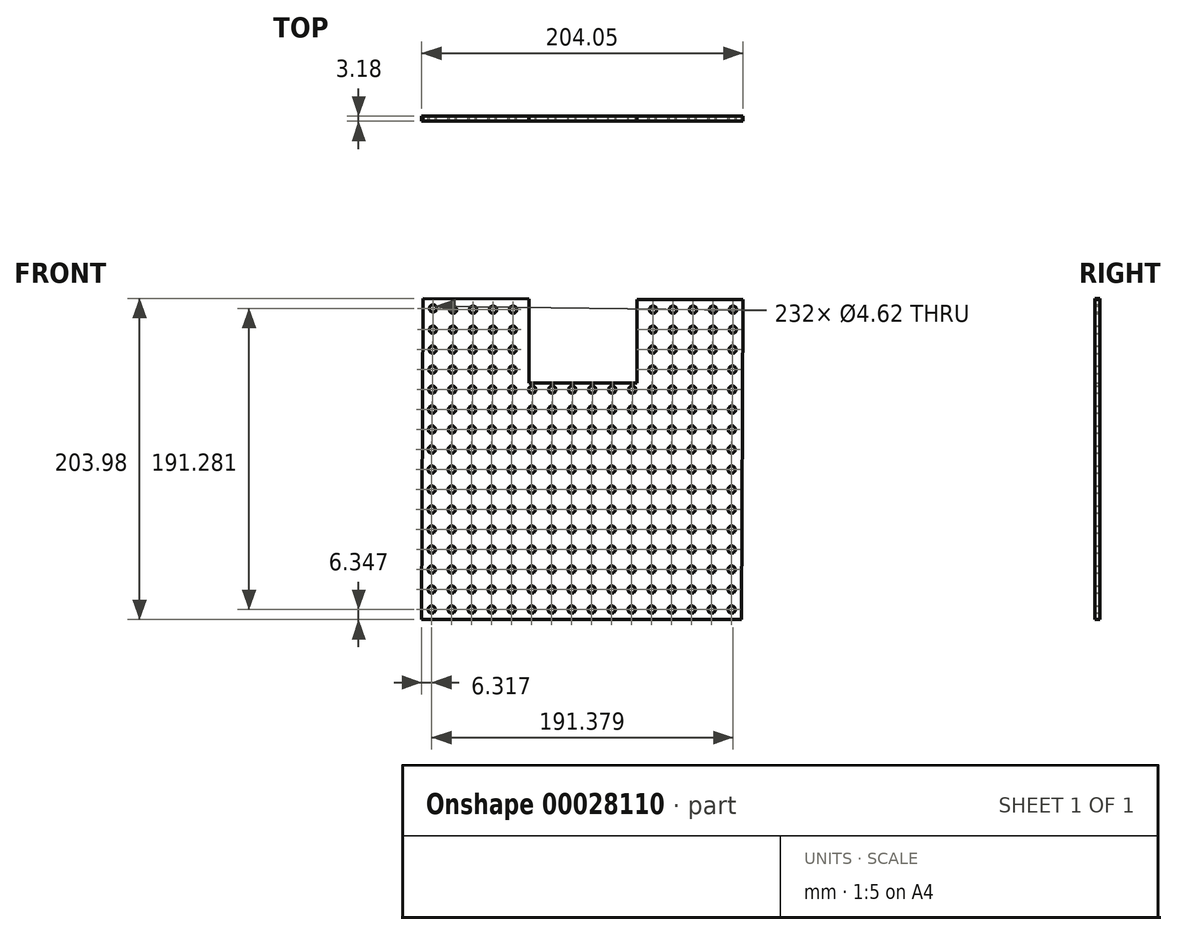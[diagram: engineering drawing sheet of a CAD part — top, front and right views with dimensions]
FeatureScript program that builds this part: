
annotation { "Feature Type Name" : "Feature", "Feature Type Description" : "" }
export const myFeature = defineFeature(function(context is Context, id is Id, definition is map)
    precondition{}
    {
        {
            var Q0;
            Q0=qCreatedBy(makeId("Front.planeOp"),FACE);
            var sketch = newSketch(context, id + "F0", { "sketchPlane" : qUnion([Q0])});
            skCircle(sketch, "E0", {"center": v(-1.82, 8.54) * mm, "radius": 2.31 * mm});
            skCircle(sketch, "E1.1.0.0", {"center": v(-14.52, 8.54) * mm, "radius": 2.31 * mm});
            skCircle(sketch, "E1.2.0.0", {"center": v(-27.22, 8.54) * mm, "radius": 2.31 * mm});
            skCircle(sketch, "E1.3.0.0", {"center": v(-39.92, 8.54) * mm, "radius": 2.31 * mm});
            skCircle(sketch, "E1.4.0.0", {"center": v(-52.62, 8.54) * mm, "radius": 2.31 * mm});
            skLineSegment(sketch, "E1.direction1", {"start": v(-1.82, 8.54) * mm, "end": v(-14.52, 8.54) * mm, "construction": true});
            skCircle(sketch, "E2.1.0.0", {"center": v(-1.95, -4.16) * mm, "radius": 2.31 * mm});
            skCircle(sketch, "E2.1.0.1", {"center": v(-14.65, -4.16) * mm, "radius": 2.31 * mm});
            skCircle(sketch, "E2.1.0.2", {"center": v(-27.35, -4.16) * mm, "radius": 2.31 * mm});
            skCircle(sketch, "E2.1.0.3", {"center": v(-40.05, -4.16) * mm, "radius": 2.31 * mm});
            skCircle(sketch, "E2.1.0.4", {"center": v(-52.75, -4.16) * mm, "radius": 2.31 * mm});
            skCircle(sketch, "E2.2.0.0", {"center": v(-2.08, -16.86) * mm, "radius": 2.31 * mm});
            skCircle(sketch, "E2.2.0.1", {"center": v(-14.78, -16.86) * mm, "radius": 2.31 * mm});
            skCircle(sketch, "E2.2.0.2", {"center": v(-27.48, -16.86) * mm, "radius": 2.31 * mm});
            skCircle(sketch, "E2.2.0.3", {"center": v(-40.18, -16.86) * mm, "radius": 2.31 * mm});
            skCircle(sketch, "E2.2.0.4", {"center": v(-52.88, -16.86) * mm, "radius": 2.31 * mm});
            skCircle(sketch, "E2.3.0.0", {"center": v(-2.2, -29.56) * mm, "radius": 2.31 * mm});
            skCircle(sketch, "E2.3.0.1", {"center": v(-14.9, -29.56) * mm, "radius": 2.31 * mm});
            skCircle(sketch, "E2.3.0.2", {"center": v(-27.6, -29.56) * mm, "radius": 2.31 * mm});
            skCircle(sketch, "E2.3.0.3", {"center": v(-40.3, -29.56) * mm, "radius": 2.31 * mm});
            skCircle(sketch, "E2.3.0.4", {"center": v(-53, -29.56) * mm, "radius": 2.31 * mm});
            skCircle(sketch, "E2.4.0.0", {"center": v(-2.33, -42.25) * mm, "radius": 2.31 * mm});
            skCircle(sketch, "E2.4.0.1", {"center": v(-15.03, -42.25) * mm, "radius": 2.31 * mm});
            skCircle(sketch, "E2.4.0.2", {"center": v(-27.73, -42.25) * mm, "radius": 2.31 * mm});
            skCircle(sketch, "E2.4.0.3", {"center": v(-40.43, -42.25) * mm, "radius": 2.31 * mm});
            skCircle(sketch, "E2.4.0.4", {"center": v(-53.13, -42.25) * mm, "radius": 2.31 * mm});
            skCircle(sketch, "E2.4.0.5", {"center": v(-65.83, -42.25) * mm, "radius": 2.31 * mm});
            skCircle(sketch, "E2.4.0.6", {"center": v(-78.53, -42.25) * mm, "radius": 2.31 * mm});
            skCircle(sketch, "E2.4.0.7", {"center": v(-91.23, -42.25) * mm, "radius": 2.31 * mm});
            skCircle(sketch, "E2.5.0.0", {"center": v(-2.45, -54.95) * mm, "radius": 2.31 * mm});
            skCircle(sketch, "E2.5.0.1", {"center": v(-15.15, -54.95) * mm, "radius": 2.31 * mm});
            skCircle(sketch, "E2.5.0.2", {"center": v(-27.85, -54.95) * mm, "radius": 2.31 * mm});
            skCircle(sketch, "E2.5.0.3", {"center": v(-40.55, -54.95) * mm, "radius": 2.31 * mm});
            skCircle(sketch, "E2.5.0.4", {"center": v(-53.25, -54.95) * mm, "radius": 2.31 * mm});
            skCircle(sketch, "E2.5.0.5", {"center": v(-65.95, -54.95) * mm, "radius": 2.31 * mm});
            skCircle(sketch, "E2.5.0.6", {"center": v(-78.65, -54.95) * mm, "radius": 2.31 * mm});
            skCircle(sketch, "E2.5.0.7", {"center": v(-91.35, -54.95) * mm, "radius": 2.31 * mm});
            skCircle(sketch, "E2.6.0.0", {"center": v(-2.58, -67.65) * mm, "radius": 2.31 * mm});
            skCircle(sketch, "E2.6.0.1", {"center": v(-15.28, -67.65) * mm, "radius": 2.31 * mm});
            skCircle(sketch, "E2.6.0.2", {"center": v(-27.98, -67.65) * mm, "radius": 2.31 * mm});
            skCircle(sketch, "E2.6.0.3", {"center": v(-40.68, -67.65) * mm, "radius": 2.31 * mm});
            skCircle(sketch, "E2.6.0.4", {"center": v(-53.38, -67.65) * mm, "radius": 2.31 * mm});
            skCircle(sketch, "E2.6.0.5", {"center": v(-66.08, -67.65) * mm, "radius": 2.31 * mm});
            skCircle(sketch, "E2.6.0.6", {"center": v(-78.78, -67.65) * mm, "radius": 2.31 * mm});
            skCircle(sketch, "E2.6.0.7", {"center": v(-91.48, -67.65) * mm, "radius": 2.31 * mm});
            skCircle(sketch, "E2.7.0.0", {"center": v(-2.7, -80.35) * mm, "radius": 2.31 * mm});
            skCircle(sketch, "E2.7.0.1", {"center": v(-15.4, -80.35) * mm, "radius": 2.31 * mm});
            skCircle(sketch, "E2.7.0.2", {"center": v(-28.1, -80.35) * mm, "radius": 2.31 * mm});
            skCircle(sketch, "E2.7.0.3", {"center": v(-40.8, -80.35) * mm, "radius": 2.31 * mm});
            skCircle(sketch, "E2.7.0.4", {"center": v(-53.5, -80.35) * mm, "radius": 2.31 * mm});
            skCircle(sketch, "E2.7.0.5", {"center": v(-66.2, -80.35) * mm, "radius": 2.31 * mm});
            skCircle(sketch, "E2.7.0.6", {"center": v(-78.9, -80.35) * mm, "radius": 2.31 * mm});
            skCircle(sketch, "E2.7.0.7", {"center": v(-91.6, -80.35) * mm, "radius": 2.31 * mm});
            skLineSegment(sketch, "E2.direction1", {"start": v(-1.82, 8.54) * mm, "end": v(-1.95, -4.16) * mm, "construction": true});
            skCircle(sketch, "E3.1.0.4", {"center": v(-103.93, -42.25) * mm, "radius": 2.31 * mm});
            skCircle(sketch, "E3.1.0.5", {"center": v(-104.05, -54.95) * mm, "radius": 2.31 * mm});
            skCircle(sketch, "E3.1.0.6", {"center": v(-104.18, -67.65) * mm, "radius": 2.31 * mm});
            skCircle(sketch, "E3.1.0.7", {"center": v(-104.3, -80.35) * mm, "radius": 2.31 * mm});
            skCircle(sketch, "E3.2.0.4", {"center": v(-116.63, -42.25) * mm, "radius": 2.31 * mm});
            skCircle(sketch, "E3.2.0.5", {"center": v(-116.75, -54.95) * mm, "radius": 2.31 * mm});
            skCircle(sketch, "E3.2.0.6", {"center": v(-116.88, -67.65) * mm, "radius": 2.31 * mm});
            skCircle(sketch, "E3.2.0.7", {"center": v(-117, -80.35) * mm, "radius": 2.31 * mm});
            skCircle(sketch, "E3.3.0.4", {"center": v(-129.33, -42.25) * mm, "radius": 2.31 * mm});
            skCircle(sketch, "E3.3.0.5", {"center": v(-129.45, -54.95) * mm, "radius": 2.31 * mm});
            skCircle(sketch, "E3.3.0.6", {"center": v(-129.58, -67.65) * mm, "radius": 2.31 * mm});
            skCircle(sketch, "E3.3.0.7", {"center": v(-129.7, -80.35) * mm, "radius": 2.31 * mm});
            skCircle(sketch, "E3.4.0.0", {"center": v(-141.52, 8.54) * mm, "radius": 2.31 * mm});
            skCircle(sketch, "E3.4.0.1", {"center": v(-141.65, -4.16) * mm, "radius": 2.31 * mm});
            skCircle(sketch, "E3.4.0.2", {"center": v(-141.78, -16.86) * mm, "radius": 2.31 * mm});
            skCircle(sketch, "E3.4.0.3", {"center": v(-141.9, -29.56) * mm, "radius": 2.31 * mm});
            skCircle(sketch, "E3.4.0.4", {"center": v(-142.03, -42.25) * mm, "radius": 2.31 * mm});
            skCircle(sketch, "E3.4.0.5", {"center": v(-142.15, -54.95) * mm, "radius": 2.31 * mm});
            skCircle(sketch, "E3.4.0.6", {"center": v(-142.28, -67.65) * mm, "radius": 2.31 * mm});
            skCircle(sketch, "E3.4.0.7", {"center": v(-142.4, -80.35) * mm, "radius": 2.31 * mm});
            skCircle(sketch, "E3.5.0.0", {"center": v(-154.22, 8.54) * mm, "radius": 2.31 * mm});
            skCircle(sketch, "E3.5.0.1", {"center": v(-154.35, -4.16) * mm, "radius": 2.31 * mm});
            skCircle(sketch, "E3.5.0.2", {"center": v(-154.48, -16.86) * mm, "radius": 2.31 * mm});
            skCircle(sketch, "E3.5.0.3", {"center": v(-154.6, -29.56) * mm, "radius": 2.31 * mm});
            skCircle(sketch, "E3.5.0.4", {"center": v(-154.73, -42.25) * mm, "radius": 2.31 * mm});
            skCircle(sketch, "E3.5.0.5", {"center": v(-154.85, -54.95) * mm, "radius": 2.31 * mm});
            skCircle(sketch, "E3.5.0.6", {"center": v(-154.98, -67.65) * mm, "radius": 2.31 * mm});
            skCircle(sketch, "E3.5.0.7", {"center": v(-155.1, -80.35) * mm, "radius": 2.31 * mm});
            skCircle(sketch, "E3.6.0.0", {"center": v(-166.92, 8.54) * mm, "radius": 2.31 * mm});
            skCircle(sketch, "E3.6.0.1", {"center": v(-167.05, -4.16) * mm, "radius": 2.31 * mm});
            skCircle(sketch, "E3.6.0.2", {"center": v(-167.18, -16.86) * mm, "radius": 2.31 * mm});
            skCircle(sketch, "E3.6.0.3", {"center": v(-167.3, -29.56) * mm, "radius": 2.31 * mm});
            skCircle(sketch, "E3.6.0.4", {"center": v(-167.43, -42.25) * mm, "radius": 2.31 * mm});
            skCircle(sketch, "E3.6.0.5", {"center": v(-167.55, -54.95) * mm, "radius": 2.31 * mm});
            skCircle(sketch, "E3.6.0.6", {"center": v(-167.68, -67.65) * mm, "radius": 2.31 * mm});
            skCircle(sketch, "E3.6.0.7", {"center": v(-167.8, -80.35) * mm, "radius": 2.31 * mm});
            skCircle(sketch, "E3.7.0.0", {"center": v(-179.62, 8.54) * mm, "radius": 2.31 * mm});
            skCircle(sketch, "E3.7.0.1", {"center": v(-179.75, -4.16) * mm, "radius": 2.31 * mm});
            skCircle(sketch, "E3.7.0.2", {"center": v(-179.88, -16.86) * mm, "radius": 2.31 * mm});
            skCircle(sketch, "E3.7.0.3", {"center": v(-180, -29.56) * mm, "radius": 2.31 * mm});
            skCircle(sketch, "E3.7.0.4", {"center": v(-180.13, -42.25) * mm, "radius": 2.31 * mm});
            skCircle(sketch, "E3.7.0.5", {"center": v(-180.25, -54.95) * mm, "radius": 2.31 * mm});
            skCircle(sketch, "E3.7.0.6", {"center": v(-180.38, -67.65) * mm, "radius": 2.31 * mm});
            skCircle(sketch, "E3.7.0.7", {"center": v(-180.5, -80.35) * mm, "radius": 2.31 * mm});
            skCircle(sketch, "E3.8.0.0", {"center": v(-192.32, 9.33) * mm, "radius": 2.31 * mm});
            skCircle(sketch, "E3.8.0.1", {"center": v(-192.45, -4.16) * mm, "radius": 2.31 * mm});
            skCircle(sketch, "E3.8.0.2", {"center": v(-192.58, -16.86) * mm, "radius": 2.31 * mm});
            skCircle(sketch, "E3.8.0.3", {"center": v(-192.7, -29.56) * mm, "radius": 2.31 * mm});
            skCircle(sketch, "E3.8.0.4", {"center": v(-192.83, -42.25) * mm, "radius": 2.31 * mm});
            skCircle(sketch, "E3.8.0.5", {"center": v(-192.95, -54.95) * mm, "radius": 2.31 * mm});
            skCircle(sketch, "E3.8.0.6", {"center": v(-193.08, -67.65) * mm, "radius": 2.31 * mm});
            skCircle(sketch, "E3.8.0.7", {"center": v(-193.2, -80.35) * mm, "radius": 2.31 * mm});
            skCircle(sketch, "E4.1.0.0", {"center": v(-193.2, -93.05) * mm, "radius": 2.31 * mm});
            skCircle(sketch, "E4.2.0.0", {"center": v(-193.2, -105.75) * mm, "radius": 2.31 * mm});
            skCircle(sketch, "E4.3.0.0", {"center": v(-193.2, -118.45) * mm, "radius": 2.31 * mm});
            skCircle(sketch, "E4.4.0.0", {"center": v(-193.19, -131.15) * mm, "radius": 2.31 * mm});
            skCircle(sketch, "E4.5.0.0", {"center": v(-193.18, -143.85) * mm, "radius": 2.31 * mm});
            skCircle(sketch, "E4.6.0.0", {"center": v(-193.18, -156.55) * mm, "radius": 2.31 * mm});
            skCircle(sketch, "E4.7.0.0", {"center": v(-193.18, -169.25) * mm, "radius": 2.31 * mm});
            skCircle(sketch, "E4.8.0.0", {"center": v(-193.17, -181.95) * mm, "radius": 2.31 * mm});
            skCircle(sketch, "E5.1.0.0", {"center": v(-180.5, -93.05) * mm, "radius": 2.31 * mm});
            skCircle(sketch, "E5.1.0.1", {"center": v(-180.5, -105.75) * mm, "radius": 2.31 * mm});
            skCircle(sketch, "E5.1.0.2", {"center": v(-180.5, -118.45) * mm, "radius": 2.31 * mm});
            skCircle(sketch, "E5.1.0.3", {"center": v(-180.49, -131.15) * mm, "radius": 2.31 * mm});
            skCircle(sketch, "E5.1.0.4", {"center": v(-180.48, -143.85) * mm, "radius": 2.31 * mm});
            skCircle(sketch, "E5.1.0.5", {"center": v(-180.48, -156.55) * mm, "radius": 2.31 * mm});
            skCircle(sketch, "E5.1.0.6", {"center": v(-180.48, -169.25) * mm, "radius": 2.31 * mm});
            skCircle(sketch, "E5.1.0.7", {"center": v(-180.47, -181.95) * mm, "radius": 2.31 * mm});
            skCircle(sketch, "E5.2.0.0", {"center": v(-167.8, -93.05) * mm, "radius": 2.31 * mm});
            skCircle(sketch, "E5.2.0.1", {"center": v(-167.8, -105.75) * mm, "radius": 2.31 * mm});
            skCircle(sketch, "E5.2.0.2", {"center": v(-167.8, -118.45) * mm, "radius": 2.31 * mm});
            skCircle(sketch, "E5.2.0.3", {"center": v(-167.79, -131.15) * mm, "radius": 2.31 * mm});
            skCircle(sketch, "E5.2.0.4", {"center": v(-167.78, -143.85) * mm, "radius": 2.31 * mm});
            skCircle(sketch, "E5.2.0.5", {"center": v(-167.78, -156.55) * mm, "radius": 2.31 * mm});
            skCircle(sketch, "E5.2.0.6", {"center": v(-167.78, -169.25) * mm, "radius": 2.31 * mm});
            skCircle(sketch, "E5.2.0.7", {"center": v(-167.77, -181.95) * mm, "radius": 2.31 * mm});
            skCircle(sketch, "E5.3.0.0", {"center": v(-155.1, -93.05) * mm, "radius": 2.31 * mm});
            skCircle(sketch, "E5.3.0.1", {"center": v(-155.1, -105.75) * mm, "radius": 2.31 * mm});
            skCircle(sketch, "E5.3.0.2", {"center": v(-155.1, -118.45) * mm, "radius": 2.31 * mm});
            skCircle(sketch, "E5.3.0.3", {"center": v(-155.09, -131.15) * mm, "radius": 2.31 * mm});
            skCircle(sketch, "E5.3.0.4", {"center": v(-155.08, -143.85) * mm, "radius": 2.31 * mm});
            skCircle(sketch, "E5.3.0.5", {"center": v(-155.08, -156.55) * mm, "radius": 2.31 * mm});
            skCircle(sketch, "E5.3.0.6", {"center": v(-155.08, -169.25) * mm, "radius": 2.31 * mm});
            skCircle(sketch, "E5.3.0.7", {"center": v(-155.07, -181.95) * mm, "radius": 2.31 * mm});
            skCircle(sketch, "E5.4.0.0", {"center": v(-142.4, -93.05) * mm, "radius": 2.31 * mm});
            skCircle(sketch, "E5.4.0.1", {"center": v(-142.4, -105.75) * mm, "radius": 2.31 * mm});
            skCircle(sketch, "E5.4.0.2", {"center": v(-142.4, -118.45) * mm, "radius": 2.31 * mm});
            skCircle(sketch, "E5.4.0.3", {"center": v(-142.39, -131.15) * mm, "radius": 2.31 * mm});
            skCircle(sketch, "E5.4.0.4", {"center": v(-142.38, -143.85) * mm, "radius": 2.31 * mm});
            skCircle(sketch, "E5.4.0.5", {"center": v(-142.38, -156.55) * mm, "radius": 2.31 * mm});
            skCircle(sketch, "E5.4.0.6", {"center": v(-142.38, -169.25) * mm, "radius": 2.31 * mm});
            skCircle(sketch, "E5.4.0.7", {"center": v(-142.37, -181.95) * mm, "radius": 2.31 * mm});
            skCircle(sketch, "E5.5.0.0", {"center": v(-129.7, -93.05) * mm, "radius": 2.31 * mm});
            skCircle(sketch, "E5.5.0.1", {"center": v(-129.7, -105.75) * mm, "radius": 2.31 * mm});
            skCircle(sketch, "E5.5.0.2", {"center": v(-129.7, -118.45) * mm, "radius": 2.31 * mm});
            skCircle(sketch, "E5.5.0.3", {"center": v(-129.69, -131.15) * mm, "radius": 2.31 * mm});
            skCircle(sketch, "E5.5.0.4", {"center": v(-129.68, -143.85) * mm, "radius": 2.31 * mm});
            skCircle(sketch, "E5.5.0.5", {"center": v(-129.68, -156.55) * mm, "radius": 2.31 * mm});
            skCircle(sketch, "E5.5.0.6", {"center": v(-129.68, -169.25) * mm, "radius": 2.31 * mm});
            skCircle(sketch, "E5.5.0.7", {"center": v(-129.67, -181.95) * mm, "radius": 2.31 * mm});
            skCircle(sketch, "E5.6.0.0", {"center": v(-117, -93.05) * mm, "radius": 2.31 * mm});
            skCircle(sketch, "E5.6.0.1", {"center": v(-117, -105.75) * mm, "radius": 2.31 * mm});
            skCircle(sketch, "E5.6.0.2", {"center": v(-117, -118.45) * mm, "radius": 2.31 * mm});
            skCircle(sketch, "E5.6.0.3", {"center": v(-116.99, -131.15) * mm, "radius": 2.31 * mm});
            skCircle(sketch, "E5.6.0.4", {"center": v(-116.98, -143.85) * mm, "radius": 2.31 * mm});
            skCircle(sketch, "E5.6.0.5", {"center": v(-116.98, -156.55) * mm, "radius": 2.31 * mm});
            skCircle(sketch, "E5.6.0.6", {"center": v(-116.98, -169.25) * mm, "radius": 2.31 * mm});
            skCircle(sketch, "E5.6.0.7", {"center": v(-116.97, -181.95) * mm, "radius": 2.31 * mm});
            skCircle(sketch, "E5.7.0.0", {"center": v(-104.3, -93.05) * mm, "radius": 2.31 * mm});
            skCircle(sketch, "E5.7.0.1", {"center": v(-104.3, -105.75) * mm, "radius": 2.31 * mm});
            skCircle(sketch, "E5.7.0.2", {"center": v(-104.3, -118.45) * mm, "radius": 2.31 * mm});
            skCircle(sketch, "E5.7.0.3", {"center": v(-104.29, -131.15) * mm, "radius": 2.31 * mm});
            skCircle(sketch, "E5.7.0.4", {"center": v(-104.28, -143.85) * mm, "radius": 2.31 * mm});
            skCircle(sketch, "E5.7.0.5", {"center": v(-104.28, -156.55) * mm, "radius": 2.31 * mm});
            skCircle(sketch, "E5.7.0.6", {"center": v(-104.28, -169.25) * mm, "radius": 2.31 * mm});
            skCircle(sketch, "E5.7.0.7", {"center": v(-104.27, -181.95) * mm, "radius": 2.31 * mm});
            skLineSegment(sketch, "E5.direction1", {"start": v(-193.2, -93.05) * mm, "end": v(-180.5, -93.05) * mm, "construction": true});
            skCircle(sketch, "E6.1.0.0", {"center": v(-91.6, -93.05) * mm, "radius": 2.31 * mm});
            skCircle(sketch, "E6.1.0.1", {"center": v(-91.6, -105.75) * mm, "radius": 2.31 * mm});
            skCircle(sketch, "E6.1.0.2", {"center": v(-91.6, -118.45) * mm, "radius": 2.31 * mm});
            skCircle(sketch, "E6.1.0.3", {"center": v(-91.59, -131.15) * mm, "radius": 2.31 * mm});
            skCircle(sketch, "E6.1.0.4", {"center": v(-91.58, -143.85) * mm, "radius": 2.31 * mm});
            skCircle(sketch, "E6.1.0.5", {"center": v(-91.58, -156.55) * mm, "radius": 2.31 * mm});
            skCircle(sketch, "E6.1.0.6", {"center": v(-91.58, -169.25) * mm, "radius": 2.31 * mm});
            skCircle(sketch, "E6.1.0.7", {"center": v(-91.57, -181.95) * mm, "radius": 2.31 * mm});
            skCircle(sketch, "E6.2.0.0", {"center": v(-78.9, -93.05) * mm, "radius": 2.31 * mm});
            skCircle(sketch, "E6.2.0.1", {"center": v(-78.9, -105.75) * mm, "radius": 2.31 * mm});
            skCircle(sketch, "E6.2.0.2", {"center": v(-78.9, -118.45) * mm, "radius": 2.31 * mm});
            skCircle(sketch, "E6.2.0.3", {"center": v(-78.89, -131.15) * mm, "radius": 2.31 * mm});
            skCircle(sketch, "E6.2.0.4", {"center": v(-78.88, -143.85) * mm, "radius": 2.31 * mm});
            skCircle(sketch, "E6.2.0.5", {"center": v(-78.88, -156.55) * mm, "radius": 2.31 * mm});
            skCircle(sketch, "E6.2.0.6", {"center": v(-78.88, -169.25) * mm, "radius": 2.31 * mm});
            skCircle(sketch, "E6.2.0.7", {"center": v(-78.87, -181.95) * mm, "radius": 2.31 * mm});
            skCircle(sketch, "E6.3.0.0", {"center": v(-66.2, -93.05) * mm, "radius": 2.31 * mm});
            skCircle(sketch, "E6.3.0.1", {"center": v(-66.2, -105.75) * mm, "radius": 2.31 * mm});
            skCircle(sketch, "E6.3.0.2", {"center": v(-66.2, -118.45) * mm, "radius": 2.31 * mm});
            skCircle(sketch, "E6.3.0.3", {"center": v(-66.19, -131.15) * mm, "radius": 2.31 * mm});
            skCircle(sketch, "E6.3.0.4", {"center": v(-66.18, -143.85) * mm, "radius": 2.31 * mm});
            skCircle(sketch, "E6.3.0.5", {"center": v(-66.18, -156.55) * mm, "radius": 2.31 * mm});
            skCircle(sketch, "E6.3.0.6", {"center": v(-66.18, -169.25) * mm, "radius": 2.31 * mm});
            skCircle(sketch, "E6.3.0.7", {"center": v(-66.17, -181.95) * mm, "radius": 2.31 * mm});
            skCircle(sketch, "E6.4.0.0", {"center": v(-53.5, -93.05) * mm, "radius": 2.31 * mm});
            skCircle(sketch, "E6.4.0.1", {"center": v(-53.5, -105.75) * mm, "radius": 2.31 * mm});
            skCircle(sketch, "E6.4.0.2", {"center": v(-53.5, -118.45) * mm, "radius": 2.31 * mm});
            skCircle(sketch, "E6.4.0.3", {"center": v(-53.49, -131.15) * mm, "radius": 2.31 * mm});
            skCircle(sketch, "E6.4.0.4", {"center": v(-53.48, -143.85) * mm, "radius": 2.31 * mm});
            skCircle(sketch, "E6.4.0.5", {"center": v(-53.48, -156.55) * mm, "radius": 2.31 * mm});
            skCircle(sketch, "E6.4.0.6", {"center": v(-53.48, -169.25) * mm, "radius": 2.31 * mm});
            skCircle(sketch, "E6.4.0.7", {"center": v(-53.47, -181.95) * mm, "radius": 2.31 * mm});
            skCircle(sketch, "E6.5.0.0", {"center": v(-40.8, -93.05) * mm, "radius": 2.31 * mm});
            skCircle(sketch, "E6.5.0.1", {"center": v(-40.8, -105.75) * mm, "radius": 2.31 * mm});
            skCircle(sketch, "E6.5.0.2", {"center": v(-40.8, -118.45) * mm, "radius": 2.31 * mm});
            skCircle(sketch, "E6.5.0.3", {"center": v(-40.79, -131.15) * mm, "radius": 2.31 * mm});
            skCircle(sketch, "E6.5.0.4", {"center": v(-40.78, -143.85) * mm, "radius": 2.31 * mm});
            skCircle(sketch, "E6.5.0.5", {"center": v(-40.78, -156.55) * mm, "radius": 2.31 * mm});
            skCircle(sketch, "E6.5.0.6", {"center": v(-40.78, -169.25) * mm, "radius": 2.31 * mm});
            skCircle(sketch, "E6.5.0.7", {"center": v(-40.77, -181.95) * mm, "radius": 2.31 * mm});
            skCircle(sketch, "E6.6.0.0", {"center": v(-28.1, -93.05) * mm, "radius": 2.31 * mm});
            skCircle(sketch, "E6.6.0.1", {"center": v(-28.1, -105.75) * mm, "radius": 2.31 * mm});
            skCircle(sketch, "E6.6.0.2", {"center": v(-28.1, -118.45) * mm, "radius": 2.31 * mm});
            skCircle(sketch, "E6.6.0.3", {"center": v(-28.09, -131.15) * mm, "radius": 2.31 * mm});
            skCircle(sketch, "E6.6.0.4", {"center": v(-28.08, -143.85) * mm, "radius": 2.31 * mm});
            skCircle(sketch, "E6.6.0.5", {"center": v(-28.08, -156.55) * mm, "radius": 2.31 * mm});
            skCircle(sketch, "E6.6.0.6", {"center": v(-28.08, -169.25) * mm, "radius": 2.31 * mm});
            skCircle(sketch, "E6.6.0.7", {"center": v(-28.07, -181.95) * mm, "radius": 2.31 * mm});
            skCircle(sketch, "E6.7.0.0", {"center": v(-15.4, -93.05) * mm, "radius": 2.31 * mm});
            skCircle(sketch, "E6.7.0.1", {"center": v(-15.4, -105.75) * mm, "radius": 2.31 * mm});
            skCircle(sketch, "E6.7.0.2", {"center": v(-15.4, -118.45) * mm, "radius": 2.31 * mm});
            skCircle(sketch, "E6.7.0.3", {"center": v(-15.39, -131.15) * mm, "radius": 2.31 * mm});
            skCircle(sketch, "E6.7.0.4", {"center": v(-15.38, -143.85) * mm, "radius": 2.31 * mm});
            skCircle(sketch, "E6.7.0.5", {"center": v(-15.38, -156.55) * mm, "radius": 2.31 * mm});
            skCircle(sketch, "E6.7.0.6", {"center": v(-15.38, -169.25) * mm, "radius": 2.31 * mm});
            skCircle(sketch, "E6.7.0.7", {"center": v(-15.37, -181.95) * mm, "radius": 2.31 * mm});
            skCircle(sketch, "E6.8.0.0", {"center": v(-2.7, -93.05) * mm, "radius": 2.31 * mm});
            skCircle(sketch, "E6.8.0.1", {"center": v(-2.7, -105.75) * mm, "radius": 2.31 * mm});
            skCircle(sketch, "E6.8.0.2", {"center": v(-2.7, -118.45) * mm, "radius": 2.31 * mm});
            skCircle(sketch, "E6.8.0.3", {"center": v(-2.69, -131.15) * mm, "radius": 2.31 * mm});
            skCircle(sketch, "E6.8.0.4", {"center": v(-2.68, -143.85) * mm, "radius": 2.31 * mm});
            skCircle(sketch, "E6.8.0.5", {"center": v(-2.68, -156.55) * mm, "radius": 2.31 * mm});
            skCircle(sketch, "E6.8.0.6", {"center": v(-2.68, -169.25) * mm, "radius": 2.31 * mm});
            skCircle(sketch, "E6.8.0.7", {"center": v(-2.67, -181.95) * mm, "radius": 2.31 * mm});
            skLineSegment(sketch, "E6.direction1", {"start": v(-104.3, -93.05) * mm, "end": v(-91.6, -93.05) * mm, "construction": true});
            skLineSegment(sketch, "E7", {"start": v(-1.82, 8.54) * mm, "end": v(4.53, 8.48) * mm, "construction": true});
            skLineSegment(sketch, "E8", {"start": v(4.53, 8.48) * mm, "end": v(4.53, 14.83) * mm, "construction": true});
            skLineSegment(sketch, "E9", {"start": v(-192.32, 9.33) * mm, "end": v(-198.67, 9.33) * mm, "construction": true});
            skLineSegment(sketch, "E10", {"start": v(-198.67, 9.33) * mm, "end": v(-198.67, 15.68) * mm, "construction": true});
            skLineSegment(sketch, "E11", {"start": v(-2.67, -181.95) * mm, "end": v(3.68, -181.95) * mm, "construction": true});
            skLineSegment(sketch, "E12", {"start": v(3.68, -181.95) * mm, "end": v(3.68, -188.3) * mm, "construction": true});
            skLineSegment(sketch, "E13", {"start": v(-193.17, -181.95) * mm, "end": v(-199.52, -181.95) * mm, "construction": true});
            skLineSegment(sketch, "E14", {"start": v(-199.52, -181.95) * mm, "end": v(-199.52, -188.3) * mm, "construction": true});
            skLineSegment(sketch, "E15", {"start": v(-180.48, -169.25) * mm, "end": v(-167.77, -181.95) * mm, "construction": true});
            skLineSegment(sketch, "E16", {"start": v(-199.52, -188.3) * mm, "end": v(3.68, -188.3) * mm});
            skLineSegment(sketch, "E17", {"start": v(3.68, -188.3) * mm, "end": v(4.53, 14.83) * mm});
            skLineSegment(sketch, "E18", {"start": v(-199.52, -188.3) * mm, "end": v(-198.67, 15.68) * mm});
            skLineSegment(sketch, "E19.top", {"start": v(-125.52, -37.98) * mm, "end": v(-68.63, -37.98) * mm});
            skLineSegment(sketch, "E19.right", {"start": v(-68.63, 15.14) * mm, "end": v(-68.63, 15.14) * mm});
            skLineSegment(sketch, "E20", {"start": v(-62.78, 15.11) * mm, "end": v(4.53, 14.83) * mm});
            skLineSegment(sketch, "E21", {"start": v(-125.52, 15.36) * mm, "end": v(-125.52, 15.37) * mm});
            skLineSegment(sketch, "E22", {"start": v(-131.36, 15.37) * mm, "end": v(-131.36, 15.37) * mm});
            skLineSegment(sketch, "E23", {"start": v(-131.36, 15.37) * mm, "end": v(-131.36, -37.98) * mm});
            skLineSegment(sketch, "E24", {"start": v(-131.36, -37.98) * mm, "end": v(-62.78, -37.98) * mm});
            skLineSegment(sketch, "E25", {"start": v(-62.78, 15.11) * mm, "end": v(-62.78, -37.98) * mm});
            skLineSegment(sketch, "E26", {"start": v(-198.67, 15.68) * mm, "end": v(-131.36, 15.37) * mm});
            skSolve(sketch);
        }
        {
            var Q0;
            Q0=makeQuery(id+"F0.imprint","IMPRINT",FACE,{"disambiguationData":[TD([[makeQuery(id+"F0.imprint","IMPRINT",EDGE,{"derivedFrom":sQuery(id+"F0.wireOp",EDGE,"E0")}),-1.0]])]});
            extrude(context, id + "F1", {"entities" : qUnion([Q0]), "depth" : 3.17 * mm});
        }
    });
